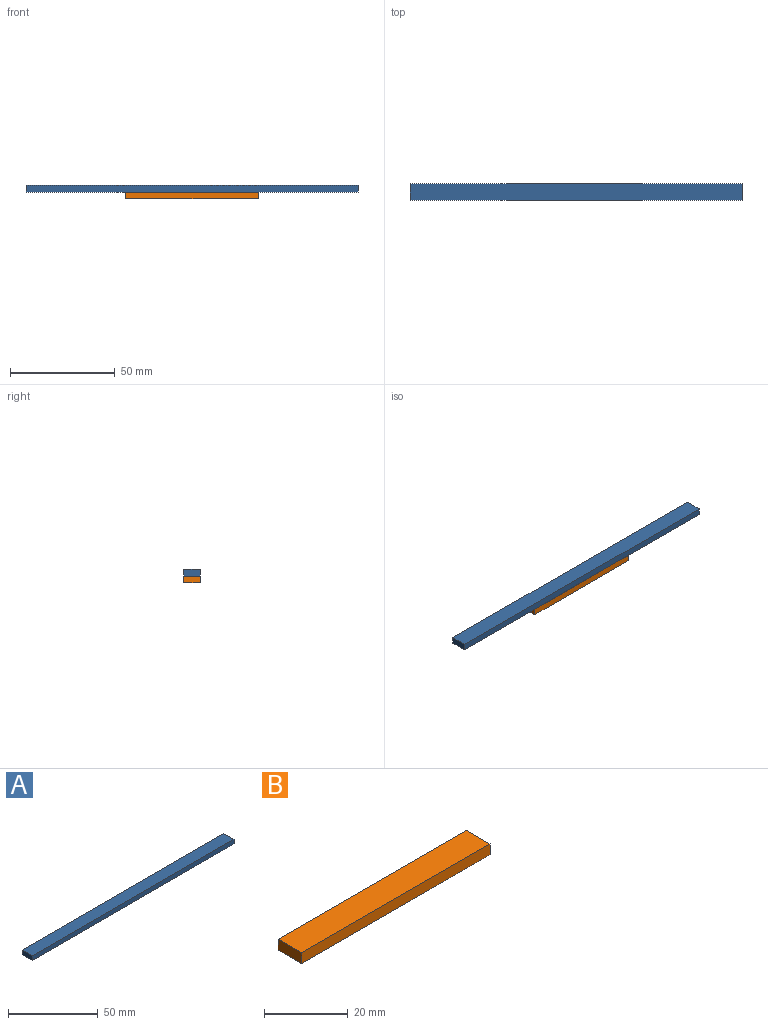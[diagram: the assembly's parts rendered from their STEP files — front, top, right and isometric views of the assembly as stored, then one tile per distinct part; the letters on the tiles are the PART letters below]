
ASSEMBLY  parts=2 mates=1
PART A: 6 faces, bbox 158.8x7.9x3.2 mm
  f0: plane 158.75x3.18mm, normal (0,1,0), area 504mm2, adj f1,f3,f4,f5
  f1: plane 7.94x3.18mm, normal (-1,0,0), area 25.2mm2, adj f0,f2,f4,f5
  f2: plane 158.75x3.18mm, normal (0,-1,0), area 504mm2, adj f1,f3,f4,f5
  f3: plane 7.94x3.18mm, normal (1,0,0), area 25.2mm2, adj f0,f2,f4,f5
  f4: plane 158.75x7.94mm, normal (0,0,1), area 1260.1mm2, adj f0,f1,f2,f3
  f5: plane 158.75x7.94mm, normal (0,0,-1), area 1260.1mm2, adj f0,f1,f2,f3
PART B: 6 faces, bbox 63.5x7.9x3.2 mm
  f0: plane 63.5x3.18mm, normal (0,1,0), area 201.6mm2, adj f1,f3,f4,f5
  f1: plane 7.94x3.18mm, normal (-1,0,0), area 25.2mm2, adj f0,f2,f4,f5
  f2: plane 63.5x3.18mm, normal (0,-1,0), area 201.6mm2, adj f1,f3,f4,f5
  f3: plane 7.94x3.18mm, normal (1,0,0), area 25.2mm2, adj f0,f2,f4,f5
  f4: plane 63.5x7.94mm, normal (0,0,1), area 504mm2, adj f0,f1,f2,f3
  f5: plane 63.5x7.94mm, normal (0,0,-1), area 504mm2, adj f0,f1,f2,f3
PLACE A t=(-5,-16.62,-4.23)mm
PLACE B t=(31.33,29.46,-7.41)mm
MATE parallel B.f4 <-> A.f5  axis (0,0,1) through (4.34,0,-4.23)mm
